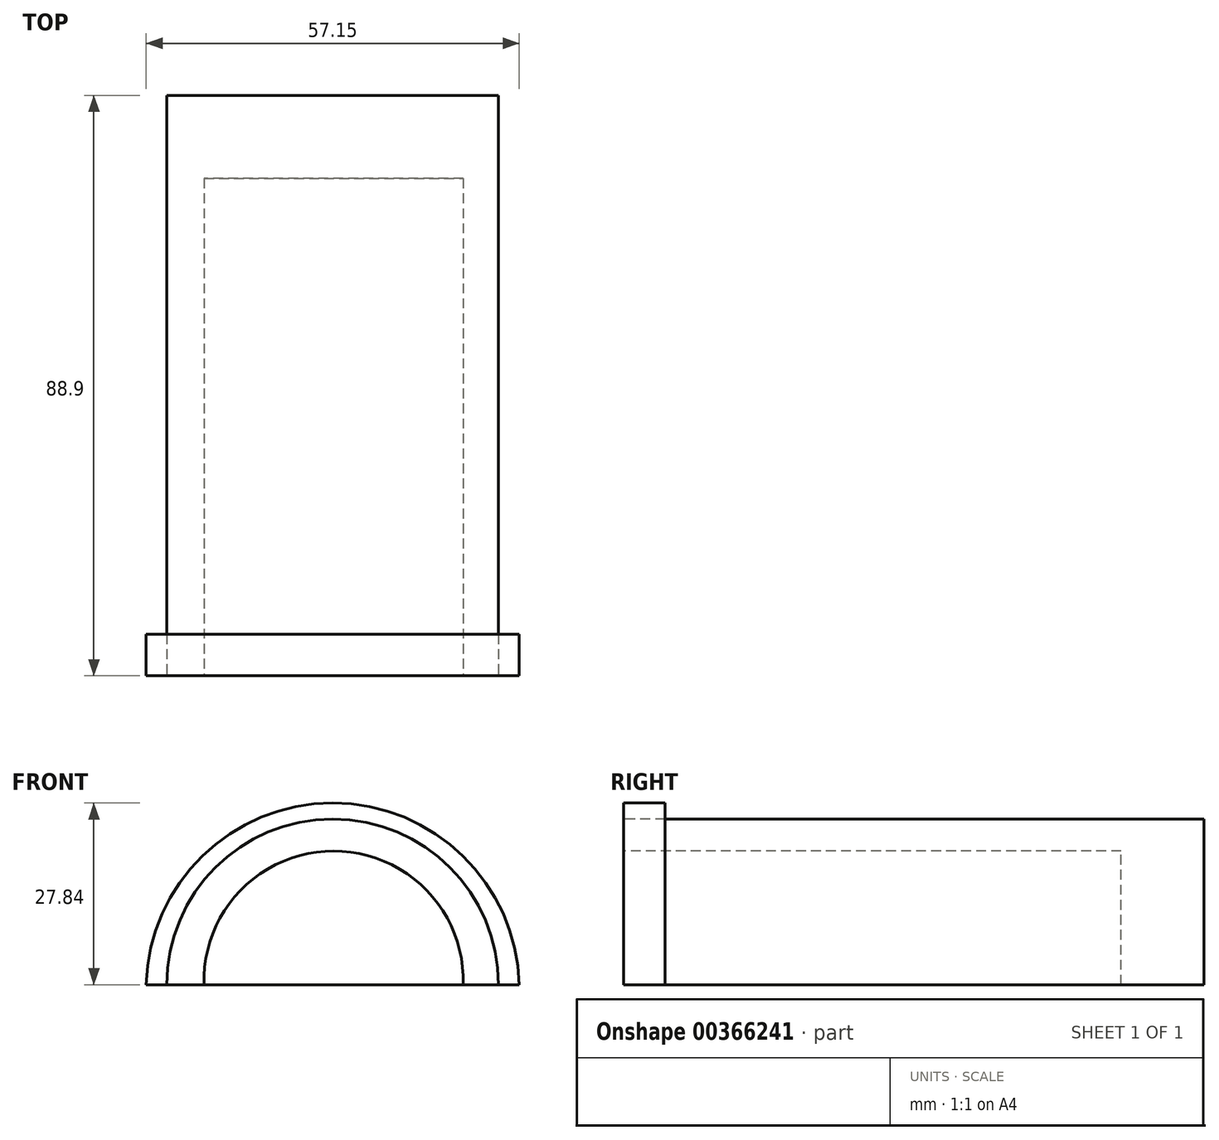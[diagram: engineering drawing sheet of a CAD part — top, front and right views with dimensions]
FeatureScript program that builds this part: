
annotation { "Feature Type Name" : "Feature", "Feature Type Description" : "" }
export const myFeature = defineFeature(function(context is Context, id is Id, definition is map)
    precondition{}
    {
        {
            var Q0;
            Q0=qCreatedBy(makeId("Front.planeOp"),FACE);
            var sketch = newSketch(context, id + "F0", { "sketchPlane" : qUnion([Q0])});
            skArc(sketch, "E0", {"start": v(25.4, 0) * mm, "mid": v(0, 25.4) * mm, "end": v(-25.4, 0) * mm});
            skLineSegment(sketch, "E1", {"start": v(-25.4, 0) * mm, "end": v(25.4, 0) * mm});
            skSolve(sketch);
        }
        {
            var Q0;
            Q0 = qSketchRegion(id + "F0", true);
            extrude(context, id + "F1", {"entities" : qUnion([Q0]), "depth" : 88.9 * mm});
        }
        {
            var Q0;
            Q0=makeQuery(id+"F1.opExtrude","CAP_FACE",FACE,{"disambiguationData":[OSD([sQuery(id+"F0.wireOp",EDGE,"E0")])],"isStart":false});
            var sketch = newSketch(context, id + "F2", { "sketchPlane" : qUnion([Q0])});
            skLineSegment(sketch, "E2", {"start": v(25.4, 0) * mm, "end": v(28.58, 0) * mm});
            skLineSegment(sketch, "E3", {"start": v(-25.4, 0) * mm, "end": v(-28.58, 0) * mm});
            skArc(sketch, "E4", {"start": v(28.58, 0) * mm, "mid": v(0, 27.84) * mm, "end": v(-28.58, 0) * mm});
            skSolve(sketch);
        }
        {
            var Q0;
            {var subQ0=sQuery(id+"F2.wireOp",EDGE,"E2");Q0=makeQuery(id+"F2.imprint","IMPRINT",FACE,{"disambiguationData":[TD([[makeQuery(id+"F2.imprint","IMPRINT",EDGE,{"derivedFrom":subQ0}),1.0]])]});}
            extrude(context, id + "F3", {"entities" : qUnion([Q0]), "oppositeDirection" : true, "depth" : 6.35 * mm});
        }
        {
            var Q0;
            Q0=makeQuery(id+"F1.opExtrude","CAP_FACE",FACE,{"disambiguationData":[OSD([sQuery(id+"F0.wireOp",EDGE,"E0"),sQuery(id+"F0.wireOp",EDGE,"E1")])],"isStart":false});
            var sketch = newSketch(context, id + "F4", { "sketchPlane" : qUnion([Q0])});
            skArc(sketch, "E5", {"start": v(20, 0) * mm, "mid": v(0.15, 20.48) * mm, "end": v(-19.7, 0) * mm});
            skSolve(sketch);
        }
        {
            var Q0;
            {var subQ0=sQuery(id+"F4.wireOp",EDGE,"E5");Q0=makeQuery(id+"F4.imprint","IMPRINT",FACE,{"disambiguationData":[TD([[makeQuery(id+"F4.imprint","IMPRINT",EDGE,{"derivedFrom":subQ0}),1.0]])]});}
            extrude(context, id + "F5", {"entities" : qUnion([Q0]), "operationType" : NewBodyOperationType.REMOVE, "oppositeDirection" : true, "depth" : 76.2 * mm});
        }
    });
